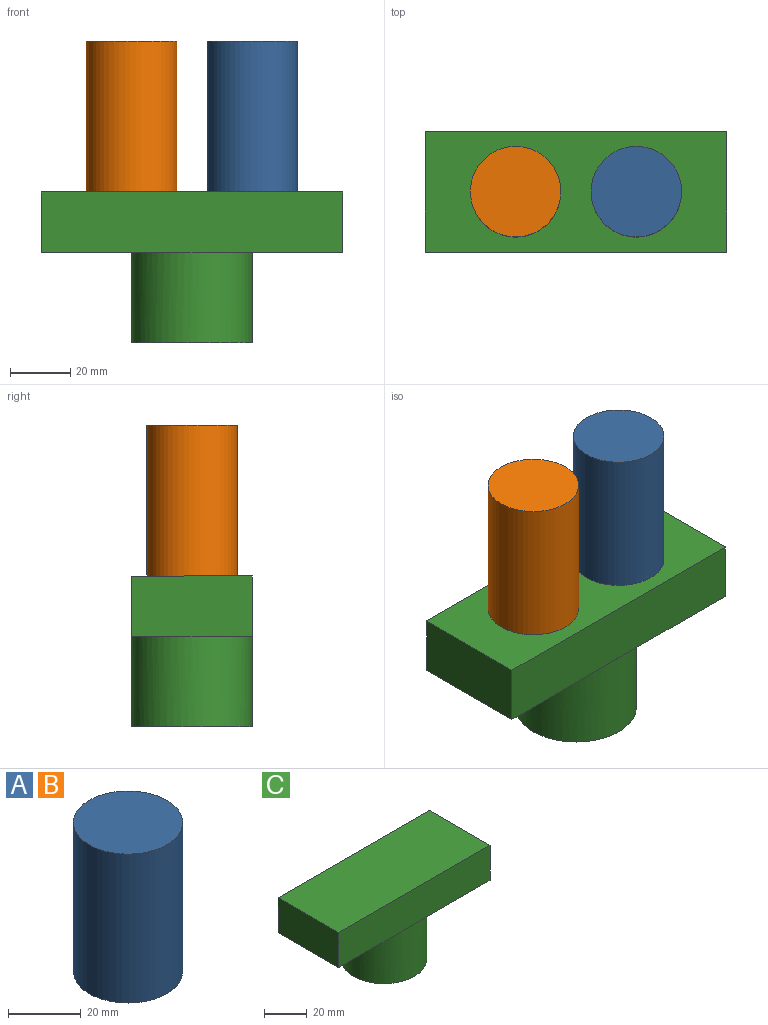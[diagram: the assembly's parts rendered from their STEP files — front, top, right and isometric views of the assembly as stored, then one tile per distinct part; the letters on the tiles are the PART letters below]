
ASSEMBLY  parts=3 mates=2
PART A: 3 faces, bbox 30x30x50 mm
  f0: cylinder r=15mm len=50mm, axis (0,0,-1), area 4712.4mm2, adj f1,f2
  f1: plane 30x30mm, normal (0,0,1), area 706.9mm2, adj f0
  f2: plane 30x30mm, normal (0,0,-1), area 706.9mm2, adj f0
PART B: same geometry as A
PART C: 9 faces, bbox 100x40x50 mm
  f0: plane 50x40mm, normal (0,0,-1), area 1371.7mm2, adj f5,f6,f7,f8
  f1: plane 40x40mm, normal (0,0,-1), area 1256.6mm2, adj f8
  f2: plane 50x40mm, normal (0,0,-1), area 1371.7mm2, adj f3,f6,f7,f8
  f3: plane 40x20mm, normal (1,0,0), area 800mm2, adj f2,f4,f6,f7
  f4: plane 100x40mm, normal (0,0,1), area 4000mm2, adj f3,f5,f6,f7
  f5: plane 40x20mm, normal (-1,0,0), area 800mm2, adj f0,f4,f6,f7
  f6: plane 100x20mm, normal (0,-1,0), area 2000mm2, adj f0,f2,f3,f4,f5
  f7: plane 100x20mm, normal (0,1,0), area 2000mm2, adj f0,f2,f3,f4,f5
  f8: cylinder r=20mm len=40mm, axis (0,0,1), area 3769.9mm2, adj f0,f1,f2
PLACE A t=(149.61,19.72,-29.17)mm
PLACE B t=(109.61,19.72,-29.17)mm
PLACE C t=(-1.93,21.93,-64.17)mm
MATE pin_slot A.f0 <-> C.f8  axis (0,0,-1) through (18.07,1.93,-29.17)mm
MATE pin_slot B.f0 <-> C.f8  axis (0,0,-1) through (-21.93,1.93,-29.17)mm
